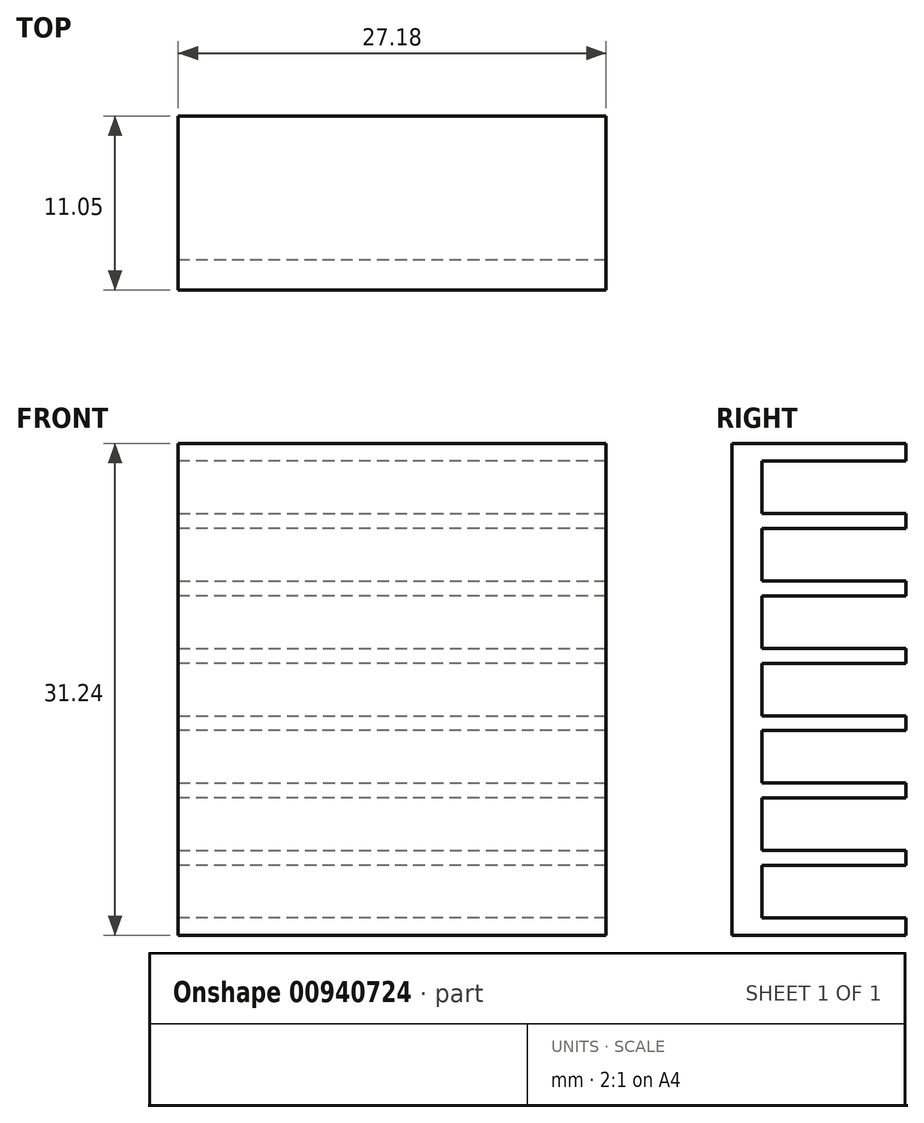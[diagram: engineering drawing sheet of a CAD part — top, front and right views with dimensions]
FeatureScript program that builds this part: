
annotation { "Feature Type Name" : "Feature", "Feature Type Description" : "" }
export const myFeature = defineFeature(function(context is Context, id is Id, definition is map)
    precondition{}
    {
        {
            var Q0;
            Q0=qCreatedBy(makeId("Front.planeOp"),FACE);
            var sketch = newSketch(context, id + "F0", { "sketchPlane" : qUnion([Q0])});
            skLineSegment(sketch, "E0.bottom", {"start": v(13.59, 15.62) * mm, "end": v(-13.59, 15.62) * mm});
            skLineSegment(sketch, "E0.top", {"start": v(13.59, -15.62) * mm, "end": v(-13.59, -15.62) * mm});
            skLineSegment(sketch, "E0.left", {"start": v(13.59, 15.62) * mm, "end": v(13.59, -15.62) * mm});
            skLineSegment(sketch, "E0.right", {"start": v(-13.59, 15.62) * mm, "end": v(-13.59, -15.62) * mm});
            skPoint(sketch, "E0.middle", {"position": v(0, 0) * mm});
            skSolve(sketch);
        }
        {
            var Q0;
            Q0=makeQuery(id+"F0.imprint","IMPRINT",FACE,{"disambiguationData":[TD([[makeQuery(id+"F0.imprint","IMPRINT",EDGE,{"derivedFrom":sQuery(id+"F0.wireOp",EDGE,"E0.bottom")}),1.0]])]});
            extrude(context, id + "F1", {"entities" : qUnion([Q0]), "depth" : 11.05 * mm, "offsetDistance" : 25.4 * mm});
        }
        {
            var Q0;
            Q0=makeQuery(id+"F1.opExtrude","CAP_FACE",FACE,{"disambiguationData":[OSD([sQuery(id+"F0.wireOp",EDGE,"E0.bottom"),sQuery(id+"F0.wireOp",EDGE,"E0.top"),sQuery(id+"F0.wireOp",EDGE,"E0.left"),sQuery(id+"F0.wireOp",EDGE,"E0.right")])],"isStart":true});
            var sketch = newSketch(context, id + "F2", { "sketchPlane" : qUnion([Q0])});
            skLineSegment(sketch, "E1", {"start": v(-13.59, 14.5) * mm, "end": v(13.59, 14.5) * mm});
            skLineSegment(sketch, "E2", {"start": v(13.59, 14.5) * mm, "end": v(13.59, 11.17) * mm});
            skLineSegment(sketch, "E3", {"start": v(13.59, 11.17) * mm, "end": v(-13.59, 11.17) * mm});
            skLineSegment(sketch, "E4", {"start": v(-13.59, 10.23) * mm, "end": v(13.59, 10.23) * mm});
            skLineSegment(sketch, "E5", {"start": v(13.59, 10.23) * mm, "end": v(13.59, 6.89) * mm});
            skLineSegment(sketch, "E6", {"start": v(13.59, 6.89) * mm, "end": v(-13.59, 6.89) * mm});
            skLineSegment(sketch, "E7", {"start": v(-13.59, 5.95) * mm, "end": v(13.59, 5.95) * mm});
            skLineSegment(sketch, "E8", {"start": v(13.59, 5.95) * mm, "end": v(13.59, 2.6) * mm});
            skLineSegment(sketch, "E9", {"start": v(13.59, 2.6) * mm, "end": v(-13.59, 2.6) * mm});
            skLineSegment(sketch, "E10", {"start": v(-13.59, 1.67) * mm, "end": v(13.59, 1.67) * mm});
            skLineSegment(sketch, "E11", {"start": v(13.59, 1.67) * mm, "end": v(13.59, -1.67) * mm});
            skLineSegment(sketch, "E12", {"start": v(13.59, -1.67) * mm, "end": v(-13.59, -1.67) * mm});
            skLineSegment(sketch, "E13", {"start": v(-13.59, -2.6) * mm, "end": v(13.59, -2.6) * mm});
            skLineSegment(sketch, "E14", {"start": v(13.59, -2.6) * mm, "end": v(13.59, -5.95) * mm});
            skLineSegment(sketch, "E15", {"start": v(13.59, -5.95) * mm, "end": v(-13.59, -5.95) * mm});
            skLineSegment(sketch, "E16", {"start": v(-13.59, -6.89) * mm, "end": v(13.59, -6.89) * mm});
            skLineSegment(sketch, "E17", {"start": v(13.59, -6.89) * mm, "end": v(13.59, -10.23) * mm});
            skLineSegment(sketch, "E18", {"start": v(13.59, -10.23) * mm, "end": v(-13.59, -10.23) * mm});
            skLineSegment(sketch, "E19", {"start": v(-13.59, -11.17) * mm, "end": v(13.59, -11.17) * mm});
            skLineSegment(sketch, "E20", {"start": v(-13.59, -14.5) * mm, "end": v(13.59, -14.5) * mm});
            skLineSegment(sketch, "E21", {"start": v(-13.59, 14.5) * mm, "end": v(-13.59, 11.17) * mm});
            skLineSegment(sketch, "E22", {"start": v(-13.59, 10.23) * mm, "end": v(-13.59, 6.89) * mm});
            skLineSegment(sketch, "E23", {"start": v(-13.59, 2.6) * mm, "end": v(-13.59, 5.95) * mm});
            skLineSegment(sketch, "E24", {"start": v(13.59, 2.6) * mm, "end": v(13.59, 5.95) * mm});
            skLineSegment(sketch, "E25", {"start": v(-13.59, 1.67) * mm, "end": v(-13.59, -1.67) * mm});
            skLineSegment(sketch, "E26", {"start": v(-13.59, -2.6) * mm, "end": v(-13.59, -5.95) * mm});
            skLineSegment(sketch, "E27", {"start": v(-13.59, -6.89) * mm, "end": v(-13.59, -10.23) * mm});
            skLineSegment(sketch, "E28", {"start": v(13.59, -11.17) * mm, "end": v(13.59, -14.5) * mm});
            skLineSegment(sketch, "E29", {"start": v(-13.59, -11.17) * mm, "end": v(-13.59, -14.5) * mm});
            skLineSegment(sketch, "E30", {"start": v(-13.59, -11.17) * mm, "end": v(-13.59, -10.23) * mm, "construction": true});
            skLineSegment(sketch, "E31", {"start": v(-13.59, -6.89) * mm, "end": v(-13.59, -5.95) * mm, "construction": true});
            skLineSegment(sketch, "E32", {"start": v(-13.59, -2.6) * mm, "end": v(-13.59, -1.67) * mm, "construction": true});
            skLineSegment(sketch, "E33", {"start": v(-13.59, 1.67) * mm, "end": v(-13.59, 2.6) * mm, "construction": true});
            skLineSegment(sketch, "E34", {"start": v(-13.59, 5.95) * mm, "end": v(-13.59, 6.89) * mm, "construction": true});
            skLineSegment(sketch, "E35", {"start": v(-13.59, 10.23) * mm, "end": v(-13.59, 11.17) * mm, "construction": true});
            skSolve(sketch);
        }
        {
            var Q0;
            Q0=makeQuery(id+"F2.imprint","IMPRINT",FACE,{"disambiguationData":[TD([[makeQuery(id+"F2.imprint","IMPRINT",EDGE,{"derivedFrom":sQuery(id+"F2.wireOp",EDGE,"E1")}),-1.0]])]});
            var Q1;
            Q1=makeQuery(id+"F2.imprint","IMPRINT",FACE,{"disambiguationData":[TD([[makeQuery(id+"F2.imprint","IMPRINT",EDGE,{"derivedFrom":sQuery(id+"F2.wireOp",EDGE,"E4")}),-1.0]])]});
            var Q2;
            Q2=makeQuery(id+"F2.imprint","IMPRINT",FACE,{"disambiguationData":[TD([[makeQuery(id+"F2.imprint","IMPRINT",EDGE,{"derivedFrom":sQuery(id+"F2.wireOp",EDGE,"E7")}),-1.0]])]});
            var Q3;
            Q3=makeQuery(id+"F2.imprint","IMPRINT",FACE,{"disambiguationData":[TD([[makeQuery(id+"F2.imprint","IMPRINT",EDGE,{"derivedFrom":sQuery(id+"F2.wireOp",EDGE,"E10")}),-1.0]])]});
            var Q4;
            Q4=makeQuery(id+"F2.imprint","IMPRINT",FACE,{"disambiguationData":[TD([[makeQuery(id+"F2.imprint","IMPRINT",EDGE,{"derivedFrom":sQuery(id+"F2.wireOp",EDGE,"E13")}),-1.0]])]});
            var Q5;
            Q5=makeQuery(id+"F2.imprint","IMPRINT",FACE,{"disambiguationData":[TD([[makeQuery(id+"F2.imprint","IMPRINT",EDGE,{"derivedFrom":sQuery(id+"F2.wireOp",EDGE,"E16")}),-1.0]])]});
            var Q6;
            Q6=makeQuery(id+"F2.imprint","IMPRINT",FACE,{"disambiguationData":[TD([[makeQuery(id+"F2.imprint","IMPRINT",EDGE,{"derivedFrom":sQuery(id+"F2.wireOp",EDGE,"E19")}),-1.0]])]});
            extrude(context, id + "F3", {"entities" : qUnion([Q0, Q1, Q2, Q3, Q4, Q5, Q6]), "operationType" : NewBodyOperationType.REMOVE, "oppositeDirection" : true, "depth" : 9.14 * mm, "offsetDistance" : 25.4 * mm});
        }
    });
